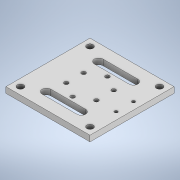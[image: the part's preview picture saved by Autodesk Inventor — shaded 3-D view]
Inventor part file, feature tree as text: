
AUTODESK INVENTOR PART (.ipt)
format: ipt  version: 2020 (Build 240168000, 168)  size: 178,176 bytes
history: native  units: in
note: dims shown in document units (in); Inventor stores cm internally (conversion verified against a paired STEP export)
features: sketch x4, projected_geometry x3, extrude x2, hole x2, pattern_circular x1
ambient origin geometry x8: Origin, YZ Plane, XZ Plane, XY Plane, X Axis, Y Axis, Z Axis, Center Point
bodies: Solid1 (feature_tree)
feature tree (12):
  extrude  "Extrusion1"  Depth=1.8125in
  hole  "Hole1"  [1 undecoded]
  pattern_circular  "Circular Pattern1"  [2 undecoded]
  extrude  "Extrusion2"  Depth=0.1875in
  hole  "Hole2"  [1 undecoded]
  sketch  "Sketch1"  dims[d0=1.8125in d1=1.8125in]
  sketch  "Sketch2"  dims[d2=0.75in d3=0.1875in]
  projected_geometry  "Projected Loop1"
  sketch  "Sketch4"  dims[d4=0.4688in]
  projected_geometry  "Projected Loop2"
  sketch  "Sketch5"  dims[d5=0.4688in d6=0.125in d7=0.0in d8=0.75in d9=0.089in d10=0.38in d11=0.172in d12=0.02in d13=0.5635in d14=0.588in d15=0.8108in d16=2.3622in d17=360.0deg d19=0.136in d20=1.5in d21=0.75in d22=1.5in d23=1.5in d24=0.125in d25=0.0in d26=0.375in d27=0.1875in d28=0.0667in d29=0.172in d30=0.172in d31=0.02in d32=0.5635in d33=0.261in d34=0.8108in]
  projected_geometry  "Projected Loop3"
note: 4 required parameter values undecoded (feature->parameter linkage not recoverable at this tier; creation-order binding heuristic only, values carry confidence <= 0.55)
